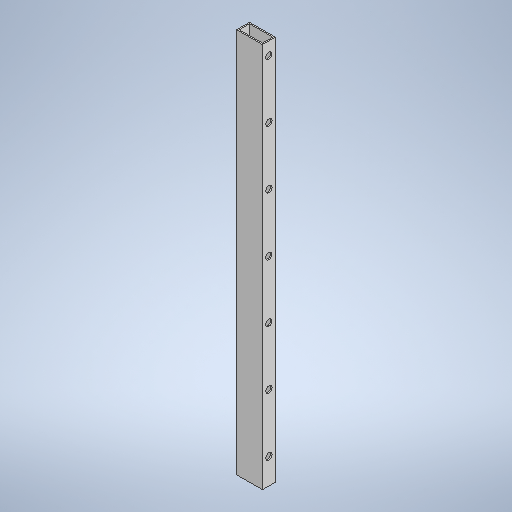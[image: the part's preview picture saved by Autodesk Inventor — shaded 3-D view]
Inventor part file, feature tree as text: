
AUTODESK INVENTOR PART (.ipt)
format: ipt  version: 2025.4 (Build 294407000, 407)  size: 278,016 bytes
history: native  units: mm
features: extrude x2, sketch x2, pattern_linear x1, projected_geometry x1
ambient origin geometry x8: Origin, YZ Plane, XZ Plane, XY Plane, X Axis, Y Axis, Z Axis, Center Point
bodies: Solid1 (feature_tree)
feature tree (6):
  extrude  "Extrusion1"  Depth=20.0mm
  extrude  "Extrusion2"  Depth=2.0mm
  pattern_linear  "Rectangular Pattern1"  Spacing1=10.0mm  [1 undecoded]
  sketch  "Sketch1"  dims[d0=40.0mm d1=20.0mm]
  sketch  "Sketch2"  dims[d2=600.0mm d3=0.0mm d4=2.0mm d5=10.0mm d6=20.0mm d7=0.0mm d8=0.0mm d9=70.0mm d11=90.0mm]
  projected_geometry  "Projected Loop1"
note: 1 required parameter value undecoded (feature->parameter linkage not recoverable at this tier; creation-order binding heuristic only, values carry confidence <= 0.55)
